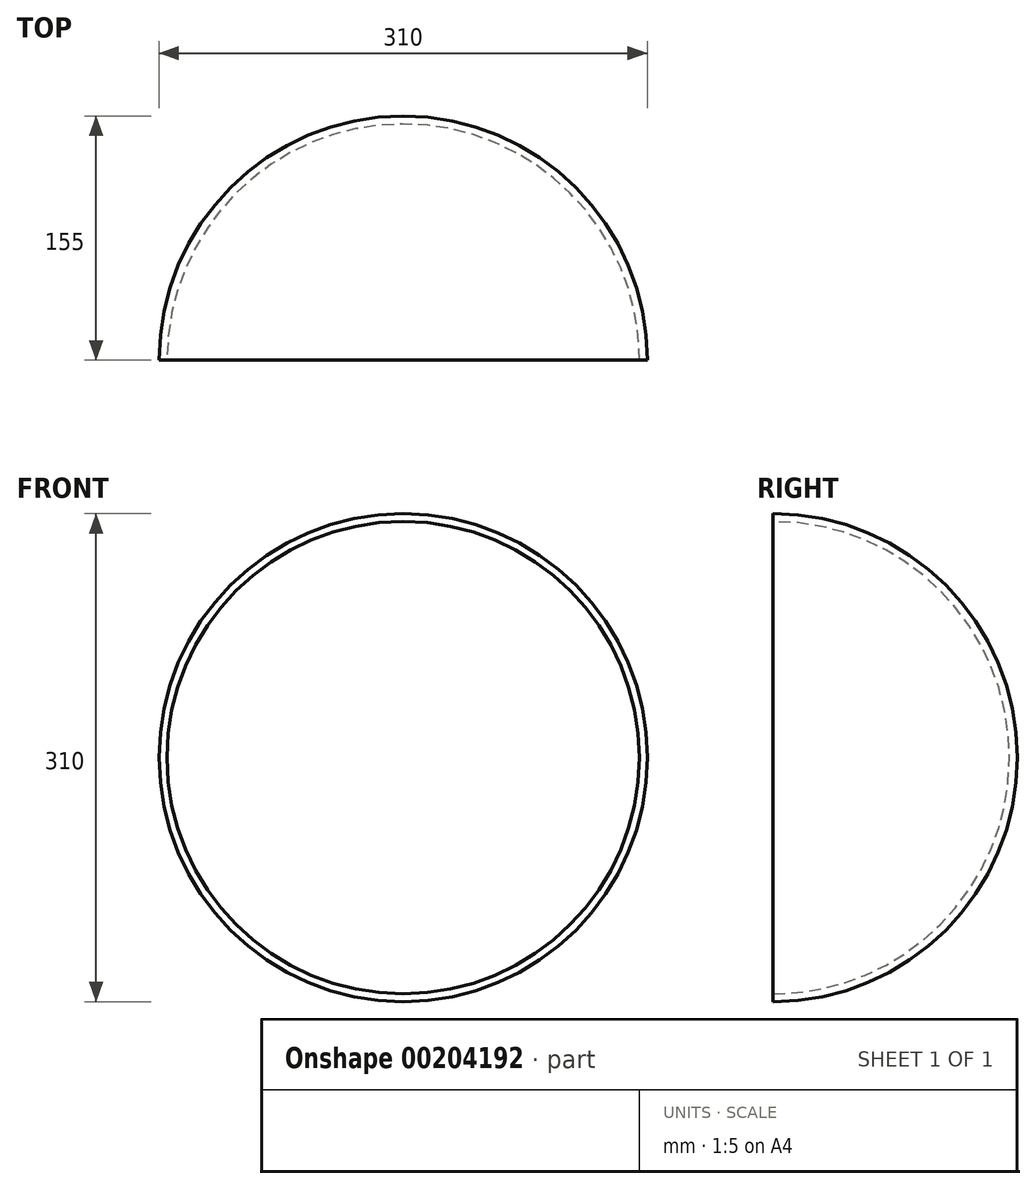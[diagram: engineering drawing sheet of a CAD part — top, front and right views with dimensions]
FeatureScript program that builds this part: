
annotation { "Feature Type Name" : "Feature", "Feature Type Description" : "" }
export const myFeature = defineFeature(function(context is Context, id is Id, definition is map)
    precondition{}
    {
        {
            var Q0;
            Q0=qCreatedBy(makeId("Front.planeOp"),FACE);
            var sketch = newSketch(context, id + "F0", { "sketchPlane" : qUnion([Q0])});
            skArc(sketch, "E0", {"start": v(0, 150) * mm, "mid": v(-150, 0) * mm, "end": v(0, -150) * mm});
            skArc(sketch, "E1.0", {"start": v(0, 155) * mm, "mid": v(-155, 0) * mm, "end": v(0, -155) * mm});
            skLineSegment(sketch, "E2", {"start": v(0, 155) * mm, "end": v(0, 150) * mm});
            skLineSegment(sketch, "E3.trimOffspring", {"start": v(0, -150) * mm, "end": v(0, -155) * mm});
            skSolve(sketch);
        }
        {
            var Q0;
            Q0 = qSketchRegion(id + "F0", true);
            var Q1;
            Q1=sQuery(id+"F0.wireOp",EDGE,"E2");
            revolve(context, id + "F1", {"entities" : qUnion([Q0]), "axis" : qUnion([Q1]), "revolveType" : RevolveType.ONE_DIRECTION, "angle" : 180 * degree});
        }
    });
